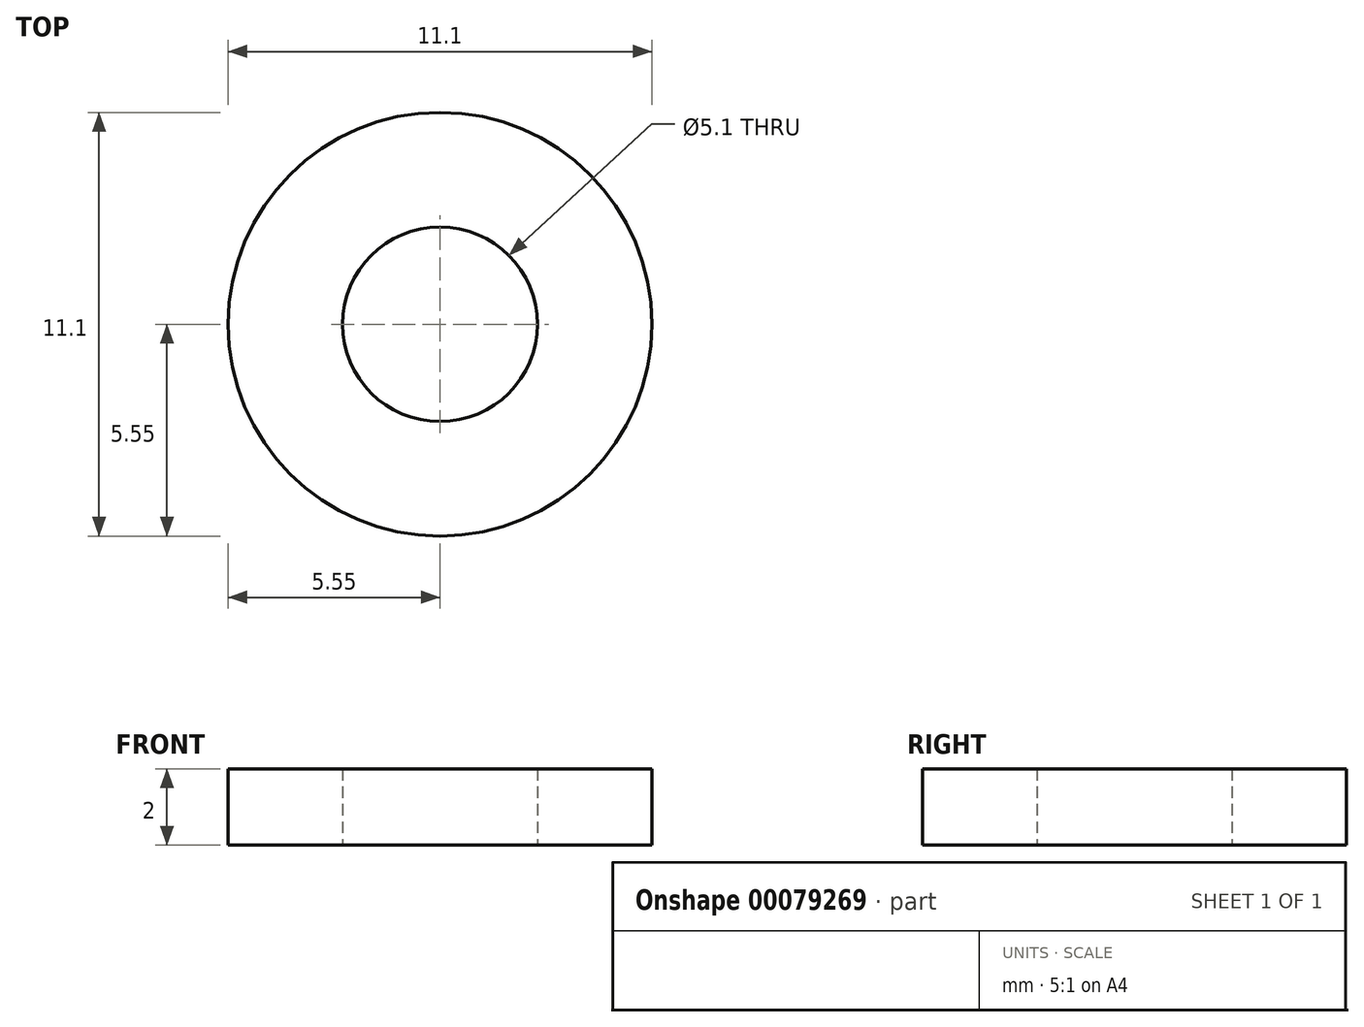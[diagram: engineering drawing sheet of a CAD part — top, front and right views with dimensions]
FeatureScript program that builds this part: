
annotation { "Feature Type Name" : "Feature", "Feature Type Description" : "" }
export const myFeature = defineFeature(function(context is Context, id is Id, definition is map)
    precondition{}
    {
        {
            var Q0;
            Q0=qCreatedBy(makeId("Top.planeOp"),FACE);
            var sketch = newSketch(context, id + "F0", { "sketchPlane" : qUnion([Q0])});
            skCircle(sketch, "E0", {"center": v(0, 0) * mm, "radius": 2.55 * mm});
            skCircle(sketch, "E1", {"center": v(0, 0) * mm, "radius": 5.55 * mm});
            skSolve(sketch);
        }
        {
            var Q0;
            Q0=qSketchRegion(id+"F0",true);
            extrude(context, id + "F1", {"entities" : qUnion([Q0]), "depth" : 2 * mm});
        }
    });
